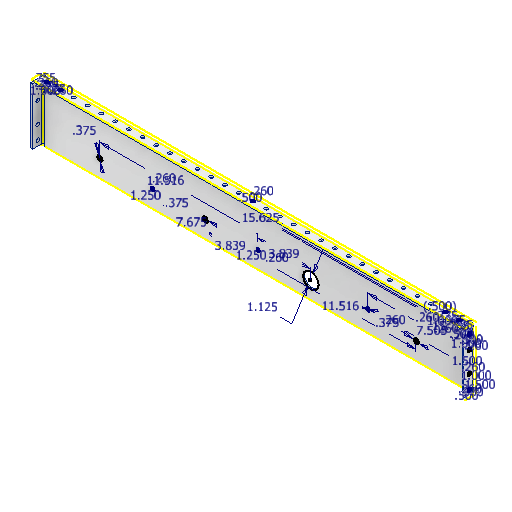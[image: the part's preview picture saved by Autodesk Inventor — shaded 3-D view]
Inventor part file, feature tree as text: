
AUTODESK INVENTOR PART (.ipt)
format: ipt  version: 2022 (Build 260153000, 153)  size: 419,328 bytes
history: native  units: in
note: dims shown in document units (in); Inventor stores cm internally (conversion verified against a paired STEP export)
features: other x12, sheet_metal_op x10, sketch x10, pattern_linear x2, projected_geometry x1
ambient origin geometry x8: Origin, YZ Plane, XZ Plane, XY Plane, X Axis, Y Axis, Z Axis, Center Point
bodies: Solid1 (feature_tree)
feature tree (35):
  sheet_metal_op  "Face1"
  sheet_metal_op  "Flange1"
  sketch  "Sketch6"  dims[d2=0.125in]
  sheet_metal_op  "Flange3"
  sheet_metal_op  "Flange4"
  sketch  "Sketch11"  dims[d5=0.25in]
  sketch  "Sketch12"  dims[d6=0.125in]
  pattern_linear  "Rectangular Pattern1"  Spacing1=0.125in  [1 undecoded]
  pattern_linear  "Rectangular Pattern2"  Spacing1=0.26in  [1 undecoded]
  sketch  "Sketch2"  dims[d0=31.51in]
  other  "Plate1"
  sketch  "Sketch3"  dims[d1=4.5in]
  other  "Plate2"
  sheet_metal_op  "Bend1"
  sheet_metal_op  "Corner1"
  projected_geometry  "Projected Loop1"
  sketch  "Sketch9"  dims[d3=0.125in]
  other  "Plate4"
  sheet_metal_op  "Bend3"
  sheet_metal_op  "Corner3"
  sketch  "Sketch10"  dims[d4=0.0625in]
  other  "Plate5"
  sheet_metal_op  "Bend4"
  sheet_metal_op  "Corner4"
  sketch  "Sketch13"  dims[d7=0.875in d8=90.0deg d9=0.125in]
  sketch  "Sketch14"  dims[d10=0.5in]
  sketch  "Sketch15"  dims[d11=0.125in d12=0.125in d23=0.26in d24=0.26in d25=1.0in d26=0.26in d27=0.755in d28=0.26in d29=1.0in d35=0.755in d66=0.375in d67=0.375in d68=0.375in d69=0.375in d77=0.125in d78=0.0625in d79=0.25in d80=0.125in d81=0.875in d82=90.0deg d83=0.125in d84=0.5in d85=0.125in d86=0.125in d87=0.125in d88=0.0625in d89=0.25in d90=0.125in d91=0.875in d92=90.0deg d93=0.125in d94=0.5in d95=0.125in d96=0.125in d98=0.26in d99=15.755in d108=0.5in d109=0.5in d118=0.26in d120=1.25in d121=1.125in d122=3.8385in d123=0.375in d124=3.8385in d125=0.375in d127=0.375in d131=0.26in d132=0.5in d133=0.5in d134=0.26in d135=0.5in d136=0.5in d139=0.125in d140=0.0in d141=5.5118in d143=1.0in d144=5.5118in d146=1.0in d147=0.125in d148=0.0in d149=0.26in d150=1.0in d151=0.26in d152=1.0in d153=1.5in d156=0.26in d157=0.5in d158=0.5in d159=0.26in d160=1.0in d161=0.5in d162=0.26in d163=1.5in d164=0.26in d165=1.0in d166=0.5in d167=0.125in d168=0.0in d169=0.125in d170=0.0in d173=11.5155in d174=11.5155in d175=0.26in d176=7.675in d177=1.25in d178=0.26in d180=0.125in d181=0.0in d184=15.625in d185=0.12in d186=0.125in d187=0.0in d188=0.25in d189=0.125in d190=0.125in d191=0.0in d192=1.5in d193=7.505in]
  other  "Cut8"
  other  "Cut9"
  other  "Cut11"
  other  "Cut12"
  other  "Cut14"
  other  "Cut15"
  other  "Cut16"
  other  "Definition1"
note: 2 required parameter values undecoded (feature->parameter linkage not recoverable at this tier; creation-order binding heuristic only, values carry confidence <= 0.55)
